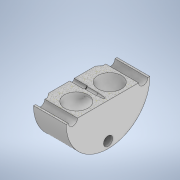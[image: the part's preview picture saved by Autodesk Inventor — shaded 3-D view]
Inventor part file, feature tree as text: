
AUTODESK INVENTOR PART (.ipt)
format: ipt  version: 2020 (Build 240168000, 168)  size: 200,704 bytes
history: native  units: mm
features: other x3, revolve x2, sketch x2
ambient origin geometry x8: Origin, YZ Plane, XZ Plane, XY Plane, X Axis, Y Axis, Z Axis, Center Point
bodies: Body1 (feature_tree)
feature tree (7):
  other  "malv2.ipt"
  revolve  "Revolution1"  Angle=90.0deg
  revolve  "Revolution2"  [1 undecoded]
  other  "Solid1::malv2.ipt"
  other  "TaggingFeature3"
  sketch  "Sketch2"  dims[d0=10.0mm d3=90.0deg]
  sketch  "Sketch3"  dims[d5=10.0mm d6=14.0mm d7=90.0deg]
note: 1 required parameter value undecoded (feature->parameter linkage not recoverable at this tier; creation-order binding heuristic only, values carry confidence <= 0.55)
